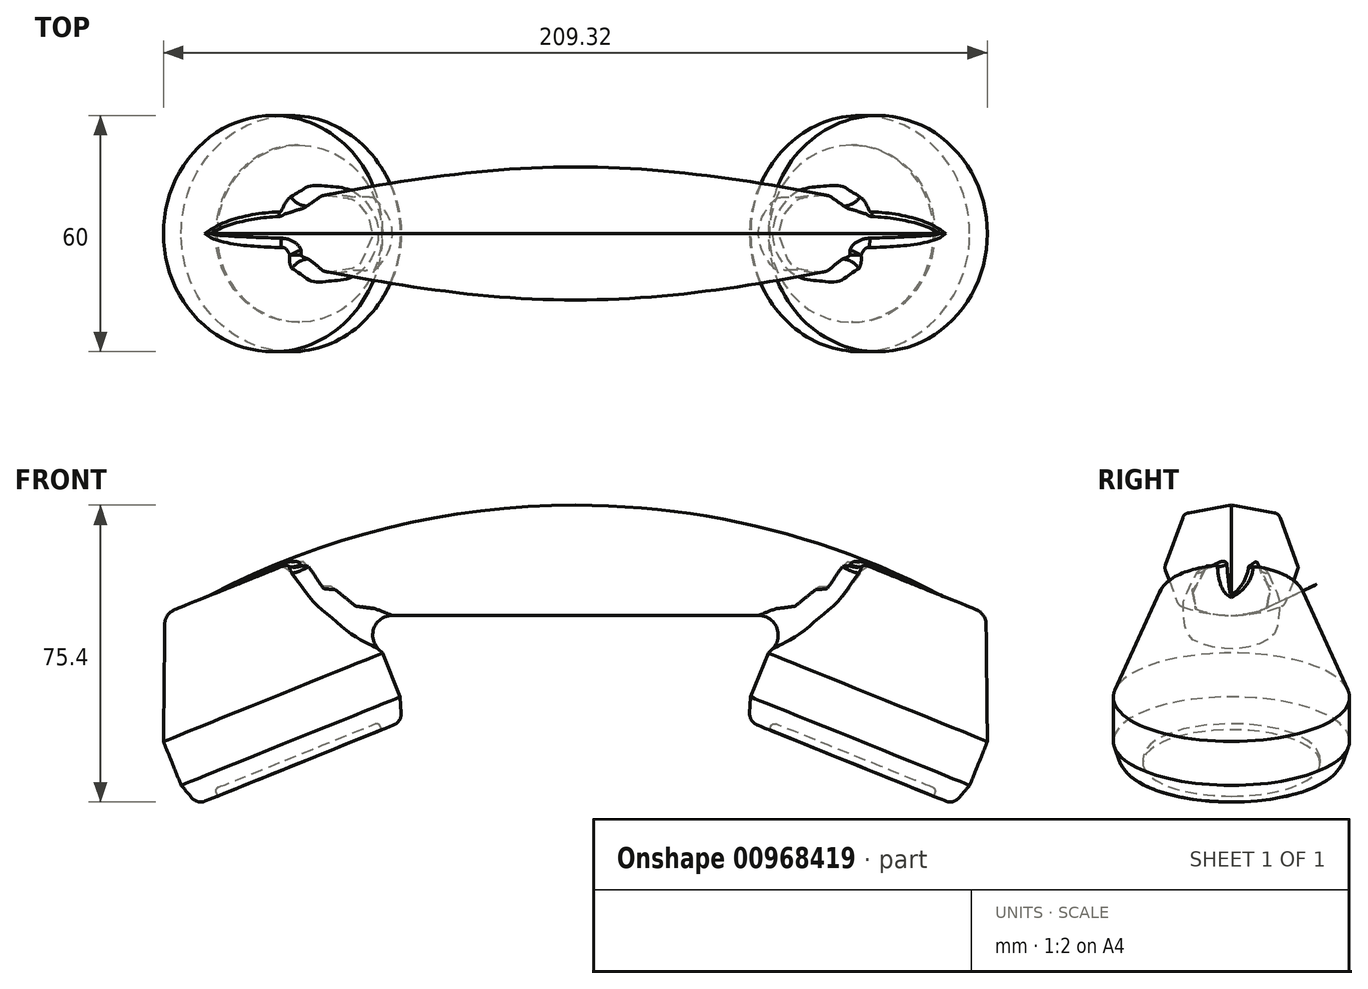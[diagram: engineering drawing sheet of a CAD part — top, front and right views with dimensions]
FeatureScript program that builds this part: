
annotation { "Feature Type Name" : "Feature", "Feature Type Description" : "" }
export const myFeature = defineFeature(function(context is Context, id is Id, definition is map)
    precondition{}
    {
        {
            var Q0;
            Q0=qCreatedBy(makeId("Right.planeOp"),FACE);
            var sketch = newSketch(context, id + "F0", { "sketchPlane" : qUnion([Q0])});
            skLineSegment(sketch, "E0", {"start": v(0, 0) * mm, "end": v(-10.86, -1.92) * mm});
            skLineSegment(sketch, "E1", {"start": v(-12.4, -3.2) * mm, "end": v(-16.75, -15.17) * mm});
            skLineSegment(sketch, "E2", {"start": v(-16.75, -16.54) * mm, "end": v(-13.85, -24.5) * mm});
            skArc(sketch, "E3", {"start": v(-12.68, -25.7) * mm, "mid": v(-6.44, -27.42) * mm, "end": v(0, -28) * mm});
            skLineSegment(sketch, "E4.MirrorCS", {"start": v(0, 0) * mm, "end": v(10.86, -1.92) * mm});
            skLineSegment(sketch, "E5.MirrorCS", {"start": v(12.4, -3.2) * mm, "end": v(16.91, -15.61) * mm});
            skLineSegment(sketch, "E6.MirrorCS", {"start": v(16.91, -16.1) * mm, "end": v(13.85, -24.5) * mm});
            skArc(sketch, "E7.MirrorCS", {"start": v(12.68, -25.7) * mm, "mid": v(6.44, -27.42) * mm, "end": v(0, -28) * mm});
            skPoint(sketch, "E8.visualSharp", {"position": v(-12, -2.12) * mm});
            skArc(sketch, "E8.filletArc", {"start": v(-10.86, -1.92) * mm, "mid": v(-11.8, -2.35) * mm, "end": v(-12.4, -3.2) * mm});
            skPoint(sketch, "E9.visualSharp", {"position": v(12, -2.12) * mm});
            skArc(sketch, "E9.filletArc", {"start": v(12.4, -3.2) * mm, "mid": v(11.8, -2.35) * mm, "end": v(10.86, -1.92) * mm});
            skPoint(sketch, "E10.visualSharp", {"position": v(13.54, -25.36) * mm});
            skArc(sketch, "E10.filletArc", {"start": v(12.68, -25.7) * mm, "mid": v(13.4, -25.23) * mm, "end": v(13.85, -24.5) * mm});
            skPoint(sketch, "E11.visualSharp", {"position": v(-13.54, -25.36) * mm});
            skArc(sketch, "E11.filletArc", {"start": v(-13.85, -24.5) * mm, "mid": v(-13.4, -25.23) * mm, "end": v(-12.68, -25.7) * mm});
            skPoint(sketch, "E12.visualSharp", {"position": v(17, -15.85) * mm});
            skArc(sketch, "E12.filletArc", {"start": v(16.91, -16.1) * mm, "mid": v(16.96, -15.85) * mm, "end": v(16.91, -15.61) * mm});
            skPoint(sketch, "E13.visualSharp", {"position": v(-17, -15.85) * mm});
            skArc(sketch, "E13.filletArc", {"start": v(-16.75, -15.17) * mm, "mid": v(-16.87, -15.85) * mm, "end": v(-16.75, -16.54) * mm});
            skSolve(sketch);
        }
        {
            var Q0;
            Q0=qCreatedBy(makeId("Front.planeOp"),FACE);
            var sketch = newSketch(context, id + "F1", { "sketchPlane" : qUnion([Q0])});
            skArc(sketch, "E14", {"start": v(0, 0) * mm, "mid": v(-48.1, -5.87) * mm, "end": v(-93.37, -23.13) * mm});
            skLineSegment(sketch, "E15", {"start": v(0, -239) * mm, "end": v(-96.56, 0) * mm, "construction": true});
            skLineSegment(sketch, "E16", {"start": v(-88.08, -21) * mm, "end": v(-101.83, -26.55) * mm});
            skLineSegment(sketch, "E17", {"start": v(-104.33, -30.22) * mm, "end": v(-104.66, -60.05) * mm});
            skLineSegment(sketch, "E18", {"start": v(-104.66, -60.05) * mm, "end": v(-100.16, -71.18) * mm});
            skLineSegment(sketch, "E19", {"start": v(-94.05, -75.18) * mm, "end": v(-90.96, -73.93) * mm});
            skLineSegment(sketch, "E20", {"start": v(-90.96, -73.93) * mm, "end": v(-91.33, -73) * mm});
            skLineSegment(sketch, "E21", {"start": v(-90.78, -71.7) * mm, "end": v(-70.85, -63.65) * mm});
            skLineSegment(sketch, "E22", {"start": v(-70.85, -63.65) * mm, "end": v(-88.08, -21) * mm});
            skPoint(sketch, "E23", {"position": v(-88.27, -20.53) * mm});
            skPoint(sketch, "E24.visualSharp", {"position": v(-91.7, -72.07) * mm});
            skArc(sketch, "E24.filletArc", {"start": v(-90.78, -71.7) * mm, "mid": v(-91.33, -72.24) * mm, "end": v(-91.33, -73) * mm});
            skPoint(sketch, "E25.visualSharp", {"position": v(-97.91, -76.74) * mm});
            skPoint(sketch, "E26.visualSharp", {"position": v(-104.3, -27.55) * mm});
            skArc(sketch, "E26.filletArc", {"start": v(-101.83, -26.55) * mm, "mid": v(-103.64, -28) * mm, "end": v(-104.33, -30.22) * mm});
            skLineSegment(sketch, "E27", {"start": v(0, -28) * mm, "end": v(-93.37, -28) * mm});
            skLineSegment(sketch, "E28", {"start": v(-93.37, -23.13) * mm, "end": v(-93.37, -28) * mm, "construction": true});
            skLineSegment(sketch, "E29.MirrorCS", {"start": v(-88.08, -21) * mm, "end": v(-74.33, -15.44) * mm});
            skLineSegment(sketch, "E30.MirrorCS", {"start": v(-69.98, -16.34) * mm, "end": v(-49.03, -37.57) * mm});
            skArc(sketch, "E31.MirrorCS", {"start": v(-74.33, -15.44) * mm, "mid": v(-72.02, -15.23) * mm, "end": v(-69.98, -16.34) * mm});
            skLineSegment(sketch, "E32.MirrorCS", {"start": v(-49.03, -37.57) * mm, "end": v(-44.53, -48.7) * mm});
            skLineSegment(sketch, "E33.MirrorCS", {"start": v(-49.24, -57.07) * mm, "end": v(-49.61, -56.14) * mm});
            skArc(sketch, "E34.MirrorCS", {"start": v(-50.91, -55.6) * mm, "mid": v(-50.15, -55.6) * mm, "end": v(-49.61, -56.14) * mm});
            skLineSegment(sketch, "E35.MirrorCS", {"start": v(-50.91, -55.6) * mm, "end": v(-70.85, -63.65) * mm});
            skLineSegment(sketch, "E36", {"start": v(-100.16, -71.18) * mm, "end": v(-97.46, -74.34) * mm});
            skLineSegment(sketch, "E37.MirrorCS", {"start": v(-46.14, -55.82) * mm, "end": v(-49.24, -57.07) * mm});
            skLineSegment(sketch, "E38.MirrorCS", {"start": v(-44.53, -48.7) * mm, "end": v(-44.27, -52.85) * mm});
            skPoint(sketch, "E39.visualSharp", {"position": v(-96.06, -75.99) * mm});
            skArc(sketch, "E39.filletArc", {"start": v(-97.46, -74.34) * mm, "mid": v(-95.9, -75.31) * mm, "end": v(-94.05, -75.18) * mm});
            skPoint(sketch, "E40.visualSharp", {"position": v(-44.14, -55.01) * mm});
            skArc(sketch, "E40.filletArc", {"start": v(-46.14, -55.82) * mm, "mid": v(-44.73, -54.64) * mm, "end": v(-44.27, -52.85) * mm});
            skSolve(sketch);
        }
        {
            var Q0;
            Q0=sQuery(id+"F1.wireOp",EDGE,"E28");
            var Q1;
            Q1=qCreatedBy(makeId("Right.planeOp"),FACE);
            cPlane(context, id + "F2", {"entities" : qUnion([Q0, Q1]), "cplaneType" : CPlaneType.LINE_ANGLE, "offset" : 25 * mm, "angle" : 0 * degree, "width" : 150 * mm, "height" : 150 * mm});
        }
        {
            var Q0;
            Q0=qCreatedBy(id+"F2.planeOp",FACE);
            var sketch = newSketch(context, id + "F3", { "sketchPlane" : qUnion([Q0])});
            skLineSegment(sketch, "E41.0", {"start": v(0, -23.13) * mm, "end": v(0, -28) * mm, "construction": true});
            skLineSegment(sketch, "E42", {"start": v(0, -23.13) * mm, "end": v(-2.17, -23.52) * mm});
            skLineSegment(sketch, "E43", {"start": v(-2.48, -23.77) * mm, "end": v(-3.38, -26.25) * mm});
            skLineSegment(sketch, "E44", {"start": v(-3.38, -26.35) * mm, "end": v(-3.1, -27.15) * mm});
            skArc(sketch, "E45", {"start": v(-2.88, -27.38) * mm, "mid": v(-1.47, -27.84) * mm, "end": v(0, -28) * mm});
            skPoint(sketch, "E46.visualSharp", {"position": v(-2.4, -23.56) * mm});
            skArc(sketch, "E46.filletArc", {"start": v(-2.17, -23.52) * mm, "mid": v(-2.36, -23.6) * mm, "end": v(-2.48, -23.77) * mm});
            skPoint(sketch, "E47.visualSharp", {"position": v(-3.03, -27.3) * mm});
            skArc(sketch, "E47.filletArc", {"start": v(-3.1, -27.15) * mm, "mid": v(-3, -27.29) * mm, "end": v(-2.88, -27.38) * mm});
            skPoint(sketch, "E48.visualSharp", {"position": v(-3.4, -26.3) * mm});
            skArc(sketch, "E48.filletArc", {"start": v(-3.38, -26.25) * mm, "mid": v(-3.4, -26.3) * mm, "end": v(-3.38, -26.35) * mm});
            skArc(sketch, "E49.MirrorCS", {"start": v(2.88, -27.38) * mm, "mid": v(1.47, -27.84) * mm, "end": v(0, -28) * mm});
            skLineSegment(sketch, "E50.MirrorCS", {"start": v(0, -23.13) * mm, "end": v(2.17, -23.52) * mm});
            skArc(sketch, "E51.MirrorCS", {"start": v(2.17, -23.52) * mm, "mid": v(2.36, -23.6) * mm, "end": v(2.48, -23.77) * mm});
            skLineSegment(sketch, "E52.MirrorCS", {"start": v(2.48, -23.77) * mm, "end": v(3.38, -26.25) * mm});
            skArc(sketch, "E53.MirrorCS", {"start": v(3.38, -26.25) * mm, "mid": v(3.4, -26.3) * mm, "end": v(3.38, -26.35) * mm});
            skLineSegment(sketch, "E54.MirrorCS", {"start": v(3.38, -26.35) * mm, "end": v(3.1, -27.15) * mm});
            skArc(sketch, "E55.MirrorCS", {"start": v(3.1, -27.15) * mm, "mid": v(3, -27.29) * mm, "end": v(2.88, -27.38) * mm});
            skSolve(sketch);
        }
        {
            var Q0;
            Q0=makeQuery(id+"F3.imprint","IMPRINT",FACE,{"disambiguationData":[TD([[makeQuery(id+"F3.imprint","IMPRINT",EDGE,{"derivedFrom":sQuery(id+"F3.wireOp",EDGE,"E42")}),1.0]])]});
            var Q1;
            Q1=makeQuery(id+"F0.imprint","IMPRINT",FACE,{"disambiguationData":[TD([[makeQuery(id+"F0.imprint","IMPRINT",EDGE,{"derivedFrom":sQuery(id+"F0.wireOp",EDGE,"E0")}),1.0]])]});
            var Q2;
            Q2=sQuery(id+"F1.wireOp",EDGE,"E14");
            var Q3;
            Q3=sQuery(id+"F1.wireOp",EDGE,"E27");
            loft(context, id + "F4", {"addGuides" : true, "endCondition" : LoftEndDerivativeType.NORMAL_TO_PROFILE, "endMagnitude" : 1, "sheetProfilesArray" : [{ "sheetProfileEntities" : qUnion([Q0]) }, { "sheetProfileEntities" : qUnion([Q1]) }], "guidesArray" : [{ "guideEntities" : qUnion([Q2]), "guideDerivativeType" : LoftGuideDerivativeType.DEFAULT, "guideDerivativeMagnitude" : 1 }, { "guideEntities" : qUnion([Q3]), "guideDerivativeType" : LoftGuideDerivativeType.DEFAULT, "guideDerivativeMagnitude" : 1 }]});
        }
        {
            var Q0;
            Q0=makeQuery(id+"F1.imprint","IMPRINT",FACE,{"disambiguationData":[TD([[makeQuery(id+"F1.imprint","IMPRINT",EDGE,{"derivedFrom":sQuery(id+"F1.wireOp",EDGE,"E17")}),1.0]])]});
            var Q1;
            Q1=sQuery(id+"F1.wireOp",EDGE,"E15");
            revolve(context, id + "F5", {"operationType" : NewBodyOperationType.ADD, "surfaceOperationType" : NewSurfaceOperationType.NEW, "entities" : qUnion([Q0]), "axis" : qUnion([Q1]), "revolveType" : RevolveType.FULL});
        }
        {
            var Q0;
            Q0=makeQuery(id+"F5.boolean.opBoolean","INTERSECT",EDGE,{"derivedFrom":[makeQuery(id+"F4.opLoft","SWEPT_FACE",FACE,{"disambiguationData":[OSD([sQuery(id+"F0.wireOp",EDGE,"E0"),sQuery(id+"F0.wireOp",EDGE,"E1"),sQuery(id+"F0.wireOp",EDGE,"E2"),sQuery(id+"F0.wireOp",EDGE,"E3"),sQuery(id+"F0.wireOp",EDGE,"E4.MirrorCS"),sQuery(id+"F0.wireOp",EDGE,"E5.MirrorCS"),sQuery(id+"F0.wireOp",EDGE,"E6.MirrorCS"),sQuery(id+"F0.wireOp",EDGE,"E7.MirrorCS"),sQuery(id+"F0.wireOp",EDGE,"E8.filletArc"),sQuery(id+"F0.wireOp",EDGE,"E9.filletArc"),sQuery(id+"F0.wireOp",EDGE,"E10.filletArc"),sQuery(id+"F0.wireOp",EDGE,"E11.filletArc"),sQuery(id+"F0.wireOp",EDGE,"E12.filletArc"),sQuery(id+"F0.wireOp",EDGE,"E13.filletArc"),sQuery(id+"F1.wireOp",VERTEX,"E14.start"),sQuery(id+"F1.wireOp",VERTEX,"E14.end"),sQuery(id+"F1.wireOp",VERTEX,"E27.start"),sQuery(id+"F1.wireOp",VERTEX,"E27.end"),sQuery(id+"F1.wireOp",EDGE,"E14"),sQuery(id+"F1.wireOp",EDGE,"E27"),sQuery(id+"F3.wireOp",EDGE,"E42"),sQuery(id+"F3.wireOp",EDGE,"E43"),sQuery(id+"F3.wireOp",EDGE,"E44"),sQuery(id+"F3.wireOp",EDGE,"E45"),sQuery(id+"F3.wireOp",EDGE,"E46.filletArc"),sQuery(id+"F3.wireOp",EDGE,"E47.filletArc"),sQuery(id+"F3.wireOp",EDGE,"E48.filletArc"),sQuery(id+"F3.wireOp",EDGE,"E49.MirrorCS"),sQuery(id+"F3.wireOp",EDGE,"E50.MirrorCS"),sQuery(id+"F3.wireOp",EDGE,"E51.MirrorCS"),sQuery(id+"F3.wireOp",EDGE,"E52.MirrorCS"),sQuery(id+"F3.wireOp",EDGE,"E53.MirrorCS"),sQuery(id+"F3.wireOp",EDGE,"E54.MirrorCS"),sQuery(id+"F3.wireOp",EDGE,"E55.MirrorCS")])]}),makeQuery(id+"F5.opRevolve","SWEPT_FACE",FACE,{"disambiguationData":[OSD([sQuery(id+"F1.wireOp",EDGE,"E17")])]})]});
            fillet(context, id + "F6", {"entities" : qUnion([Q0]), "radius" : 5 * mm, "tangentPropagation" : true, "allowEdgeOverflow" : false});
        }
        {
            var Q0;
            Q0=makeQuery(id+"F4.opLoft","SWEPT_BODY",BODY,{"disambiguationData":[OSD([makeQuery(id+"F0.imprint","IMPRINT",FACE,{"disambiguationData":[TD([[makeQuery(id+"F0.imprint","IMPRINT",EDGE,{"derivedFrom":sQuery(id+"F0.wireOp",EDGE,"E0")}),1.0]])]}),sQuery(id+"F1.wireOp",EDGE,"E14"),sQuery(id+"F1.wireOp",EDGE,"E27"),makeQuery(id+"F3.imprint","IMPRINT",FACE,{"disambiguationData":[TD([[makeQuery(id+"F3.imprint","IMPRINT",EDGE,{"derivedFrom":sQuery(id+"F3.wireOp",EDGE,"E42")}),1.0]])]})])]});
            var Q1;
            Q1=qCreatedBy(makeId("Right.planeOp"),FACE);
            mirror(context, id + "F7", {"operationType" : NewBodyOperationType.ADD, "entities" : qUnion([Q0]), "mirrorPlane" : qUnion([Q1])});
        }
    });
